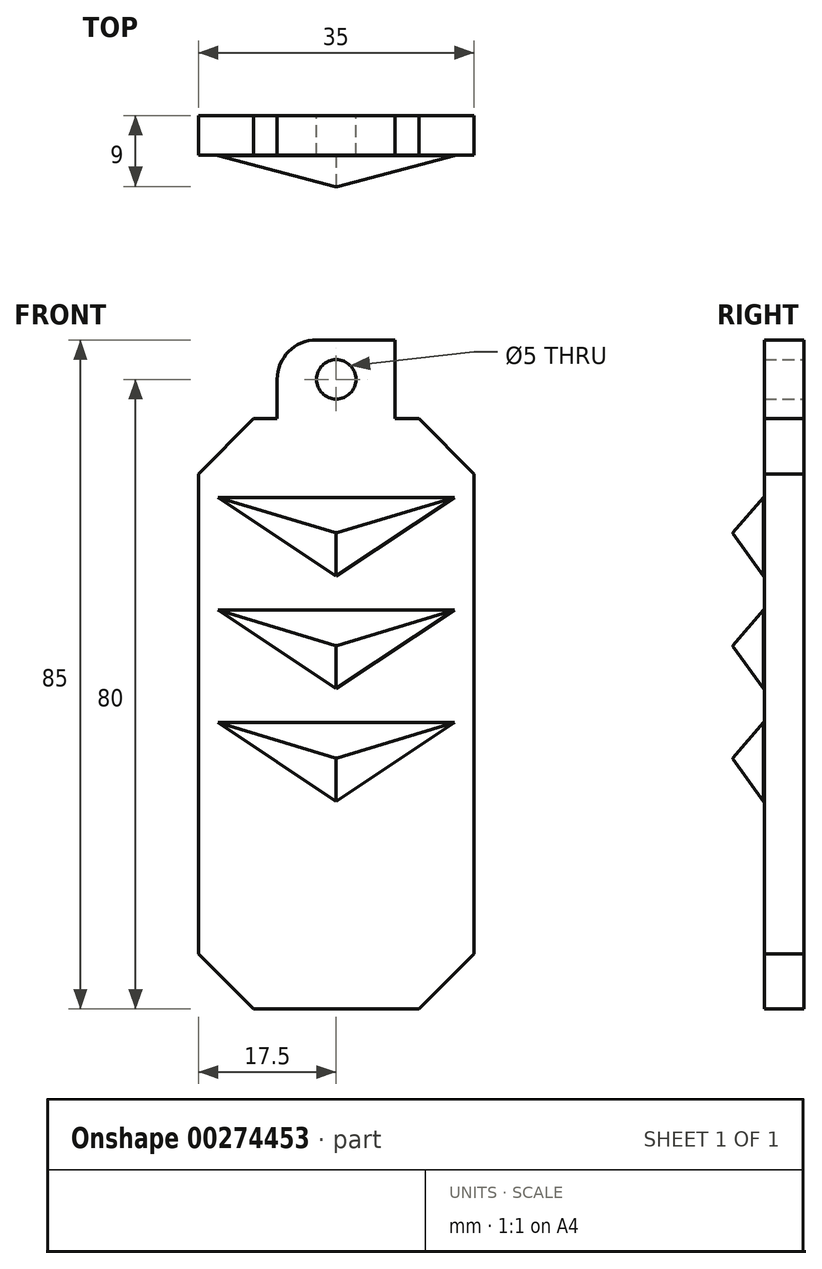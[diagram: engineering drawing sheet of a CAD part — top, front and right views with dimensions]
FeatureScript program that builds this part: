
annotation { "Feature Type Name" : "Feature", "Feature Type Description" : "" }
export const myFeature = defineFeature(function(context is Context, id is Id, definition is map)
    precondition{}
    {
        {
            var Q0;
            Q0=qCreatedBy(makeId("Front.planeOp"),FACE);
            var sketch = newSketch(context, id + "F0", { "sketchPlane" : qUnion([Q0])});
            skLineSegment(sketch, "E0.bottom", {"start": v(17.5, 37.5) * mm, "end": v(-17.5, 37.5) * mm});
            skLineSegment(sketch, "E0.top", {"start": v(17.5, -37.5) * mm, "end": v(-17.5, -37.5) * mm});
            skLineSegment(sketch, "E0.left", {"start": v(17.5, 37.5) * mm, "end": v(17.5, -37.5) * mm});
            skLineSegment(sketch, "E0.right", {"start": v(-17.5, 37.5) * mm, "end": v(-17.5, -37.5) * mm});
            skPoint(sketch, "E0.middle", {"position": v(0, 0) * mm});
            skLineSegment(sketch, "E1.bottom", {"start": v(7.5, 47.5) * mm, "end": v(0, 47.5) * mm});
            skLineSegment(sketch, "E1.left", {"start": v(7.5, 47.5) * mm, "end": v(7.5, 37.5) * mm});
            skLineSegment(sketch, "E1.right", {"start": v(-7.5, 47.5) * mm, "end": v(-7.5, 37.5) * mm});
            skPoint(sketch, "E1.middle", {"position": v(0, 37.5) * mm});
            skLineSegment(sketch, "E2", {"start": v(0, 37.5) * mm, "end": v(0, 47.5) * mm, "construction": true});
            skCircle(sketch, "E3", {"center": v(0, 42.5) * mm, "radius": 2.5 * mm});
            skLineSegment(sketch, "E4", {"start": v(-15, 27.5) * mm, "end": v(15, 27.5) * mm});
            skLineSegment(sketch, "E5", {"start": v(15, 27.5) * mm, "end": v(0, 17.5) * mm});
            skLineSegment(sketch, "E6", {"start": v(0, 17.5) * mm, "end": v(-15, 27.5) * mm});
            skLineSegment(sketch, "E7.0.1.0", {"start": v(-15, 13.2) * mm, "end": v(15, 13.2) * mm});
            skLineSegment(sketch, "E7.0.1.1", {"start": v(15, 13.2) * mm, "end": v(0, 3.2) * mm});
            skLineSegment(sketch, "E7.0.1.2", {"start": v(0, 3.2) * mm, "end": v(-15, 13.2) * mm});
            skLineSegment(sketch, "E7.0.2.0", {"start": v(-15, -1.1) * mm, "end": v(15, -1.1) * mm});
            skLineSegment(sketch, "E7.0.2.1", {"start": v(15, -1.1) * mm, "end": v(0, -11.1) * mm});
            skLineSegment(sketch, "E7.0.2.2", {"start": v(0, -11.1) * mm, "end": v(-15, -1.1) * mm});
            skLineSegment(sketch, "E7.direction1", {"start": v(-15, 27.5) * mm, "end": v(20.6, 27.5) * mm, "construction": true});
            skLineSegment(sketch, "E7.direction2", {"start": v(-15, 27.5) * mm, "end": v(-15, 13.2) * mm, "construction": true});
            skLineSegment(sketch, "E8.bottom", {"start": v(0, 37.5) * mm, "end": v(7.5, 37.5) * mm});
            skLineSegment(sketch, "E8.top", {"start": v(-7.5, 47.5) * mm, "end": v(7.5, 47.5) * mm});
            skLineSegment(sketch, "E8.left", {"start": v(-7.5, 37.5) * mm, "end": v(-7.5, 47.5) * mm});
            skLineSegment(sketch, "E8.right", {"start": v(7.5, 37.5) * mm, "end": v(7.5, 47.5) * mm});
            skLineSegment(sketch, "E9.bottom", {"start": v(-7.5, 37.5) * mm, "end": v(0, 37.5) * mm});
            skPoint(sketch, "E1.top.end.orphan", {"position": v(-7.5, 27.5) * mm});
            skPoint(sketch, "E10.trimOffspring.end.orphan", {"position": v(7.5, 27.5) * mm});
            skLineSegment(sketch, "E11", {"start": v(0, 37.5) * mm, "end": v(0, 27.5) * mm, "construction": true});
            skSolve(sketch);
        }
        {
            var Q0;
            Q0=makeQuery(id+"F0.imprint","IMPRINT",FACE,{"disambiguationData":[TD([[makeQuery(id+"F0.imprint","IMPRINT",EDGE,{"derivedFrom":sQuery(id+"F0.wireOp",EDGE,"E0.top")}),-1.0]])]});
            var Q1;
            {var subQ5=sQuery(id+"F0.wireOp",EDGE,"E1.bottom");Q1=makeQuery(id+"F0.imprint","IMPRINT",FACE,{"disambiguationData":[TD([[makeQuery(id+"F0.imprint","IMPRINT",EDGE,{"derivedFrom":subQ5}),1.0]])]});}
            var Q2;
            {var subQ5=sQuery(id+"F0.wireOp",EDGE,"E1.top");Q2=makeQuery(id+"F0.imprint","IMPRINT",FACE,{"disambiguationData":[TD([[makeQuery(id+"F0.imprint","IMPRINT",EDGE,{"derivedFrom":subQ5}),-1.0]])]});}
            var Q3;
            Q3=makeQuery(id+"F0.imprint","IMPRINT",FACE,{"disambiguationData":[TD([[makeQuery(id+"F0.imprint","IMPRINT",EDGE,{"derivedFrom":sQuery(id+"F0.wireOp",EDGE,"E3")}),-1.0]])]});
            extrude(context, id + "F1", {"entities" : qUnion([Q0, Q1, Q2, Q3]), "depth" : 5 * mm});
        }
        {
            var Q0;
            Q0=makeQuery(id+"F1.opExtrude","SWEPT_EDGE",EDGE,{"disambiguationData":[OSD([sQuery(id+"F0.wireOp",EDGE,"E0.bottom"),sQuery(id+"F0.wireOp",EDGE,"E0.right")])]});
            var Q1;
            Q1=makeQuery(id+"F1.opExtrude","SWEPT_EDGE",EDGE,{"disambiguationData":[OSD([sQuery(id+"F0.wireOp",EDGE,"E0.bottom"),sQuery(id+"F0.wireOp",EDGE,"E0.left")])]});
            var Q2;
            Q2=makeQuery(id+"F1.opExtrude","SWEPT_EDGE",EDGE,{"disambiguationData":[OSD([sQuery(id+"F0.wireOp",EDGE,"E0.top"),sQuery(id+"F0.wireOp",EDGE,"E0.right")])]});
            var Q3;
            Q3=makeQuery(id+"F1.opExtrude","SWEPT_EDGE",EDGE,{"disambiguationData":[OSD([sQuery(id+"F0.wireOp",EDGE,"E0.top"),sQuery(id+"F0.wireOp",EDGE,"E0.left")])]});
            chamfer(context, id + "F2", {"entities" : qUnion([Q0, Q1, Q2, Q3]), "width" : 7 * mm, "tangentPropagation" : true});
        }
        {
            var Q0;
            Q0=makeQuery(id+"F0.imprint","IMPRINT",FACE,{"disambiguationData":[TD([[makeQuery(id+"F0.imprint","IMPRINT",EDGE,{"derivedFrom":sQuery(id+"F0.wireOp",EDGE,"E3")}),1.0]])]});
            extrude(context, id + "F3", {"entities" : qUnion([Q0]), "operationType" : NewBodyOperationType.REMOVE, "oppositeDirection" : true, "depth" : 10 * mm});
        }
        {
            var Q0;
            Q0=makeQuery(id+"F1.opExtrude","SWEPT_EDGE",EDGE,{"disambiguationData":[OSD([sQuery(id+"F0.wireOp",EDGE,"E8.top"),sQuery(id+"F0.wireOp",EDGE,"E8.left")])]});
            var Q1;
            Q1=makeQuery(id+"F1.opExtrude","SWEPT_EDGE",EDGE,{"disambiguationData":[OSD([sQuery(id+"F0.wireOp",EDGE,"E8.top"),sQuery(id+"F0.wireOp",EDGE,"E8.right")])]});
            fillet(context, id + "F4", {"entities" : qUnion([Q0, Q1]), "radius" : 5 * mm, "tangentPropagation" : true, "allowEdgeOverflow" : false});
        }
        {
            var Q0;
            Q0=makeQuery(id+"F0.imprint","IMPRINT",FACE,{"disambiguationData":[TD([[makeQuery(id+"F0.imprint","IMPRINT",EDGE,{"derivedFrom":sQuery(id+"F0.wireOp",EDGE,"E4")}),-1.0]])]});
            var Q1;
            Q1=makeQuery(id+"F0.imprint","IMPRINT",FACE,{"disambiguationData":[TD([[makeQuery(id+"F0.imprint","IMPRINT",EDGE,{"derivedFrom":sQuery(id+"F0.wireOp",EDGE,"E7.0.1.0")}),-1.0]])]});
            var Q2;
            Q2=makeQuery(id+"F0.imprint","IMPRINT",FACE,{"disambiguationData":[TD([[makeQuery(id+"F0.imprint","IMPRINT",EDGE,{"derivedFrom":sQuery(id+"F0.wireOp",EDGE,"E7.0.2.0")}),-1.0]])]});
            extrude(context, id + "F5", {"entities" : qUnion([Q0, Q1, Q2]), "operationType" : NewBodyOperationType.ADD, "depth" : 9 * mm});
        }
        {
            var Q0;
            Q0=makeQuery(id+"F5.opExtrude","CAP_EDGE",EDGE,{"disambiguationData":[OSD([sQuery(id+"F0.wireOp",EDGE,"E4")])],"isStart":false});
            var Q1;
            Q1=makeQuery(id+"F5.opExtrude","CAP_EDGE",EDGE,{"disambiguationData":[OSD([sQuery(id+"F0.wireOp",EDGE,"E6")])],"isStart":false});
            var Q2;
            Q2=makeQuery(id+"F5.opExtrude","CAP_EDGE",EDGE,{"disambiguationData":[OSD([sQuery(id+"F0.wireOp",EDGE,"E5")])],"isStart":false});
            var Q3;
            Q3=makeQuery(id+"F5.opExtrude","CAP_EDGE",EDGE,{"disambiguationData":[OSD([sQuery(id+"F0.wireOp",EDGE,"E7.0.1.0")])],"isStart":false});
            var Q4;
            Q4=makeQuery(id+"F5.opExtrude","CAP_EDGE",EDGE,{"disambiguationData":[OSD([sQuery(id+"F0.wireOp",EDGE,"E7.0.1.2")])],"isStart":false});
            var Q5;
            Q5=makeQuery(id+"F5.opExtrude","CAP_EDGE",EDGE,{"disambiguationData":[OSD([sQuery(id+"F0.wireOp",EDGE,"E7.0.1.1")])],"isStart":false});
            var Q6;
            Q6=makeQuery(id+"F5.opExtrude","CAP_EDGE",EDGE,{"disambiguationData":[OSD([sQuery(id+"F0.wireOp",EDGE,"E7.0.2.0")])],"isStart":false});
            var Q7;
            Q7=makeQuery(id+"F5.opExtrude","CAP_EDGE",EDGE,{"disambiguationData":[OSD([sQuery(id+"F0.wireOp",EDGE,"E7.0.2.2")])],"isStart":false});
            var Q8;
            Q8=makeQuery(id+"F5.opExtrude","CAP_EDGE",EDGE,{"disambiguationData":[OSD([sQuery(id+"F0.wireOp",EDGE,"E7.0.2.1")])],"isStart":false});
            chamfer(context, id + "F6", {"entities" : qUnion([Q0, Q1, Q2, Q3, Q4, Q5, Q6, Q7, Q8]), "chamferType" : ChamferType.OFFSET_ANGLE, "width" : 3.9 * mm, "oppositeDirection" : false, "angle" : 49 * degree, "tangentPropagation" : true});
        }
    });
